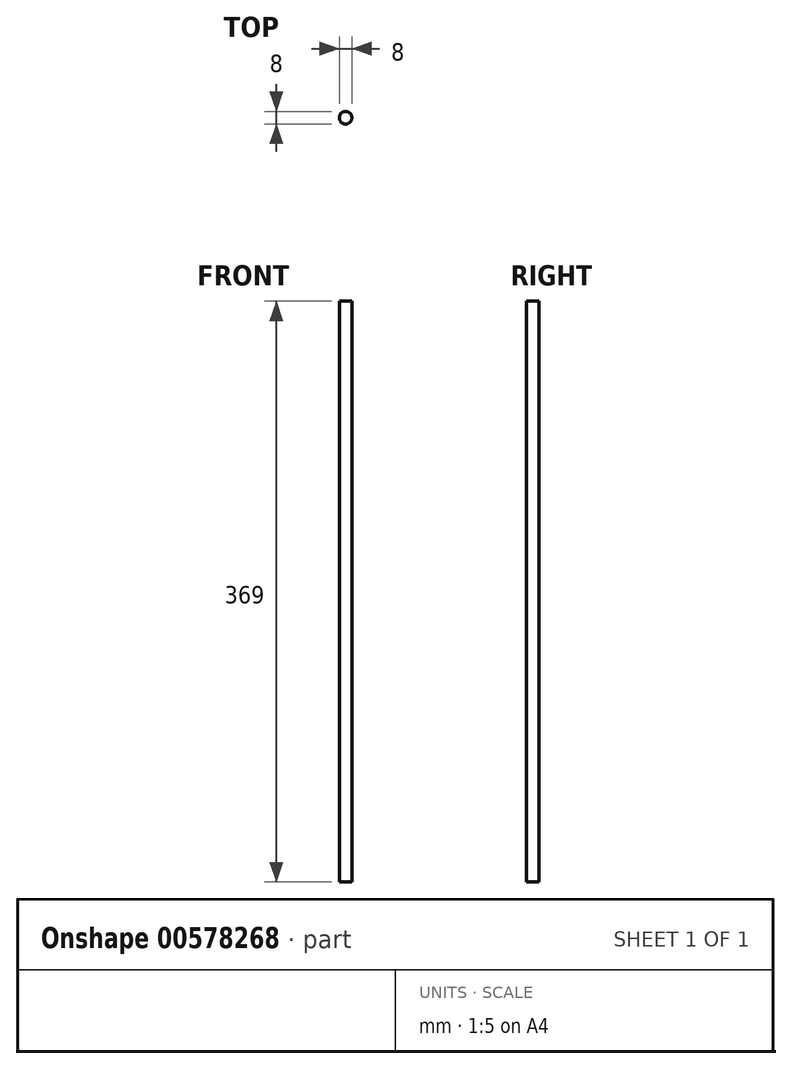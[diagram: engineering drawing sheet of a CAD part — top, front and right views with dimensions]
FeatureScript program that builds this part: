
annotation { "Feature Type Name" : "Feature", "Feature Type Description" : "" }
export const myFeature = defineFeature(function(context is Context, id is Id, definition is map)
    precondition{}
    {
        {
            var Q0;
            Q0=qCreatedBy(makeId("Top.planeOp"),FACE);
            var sketch = newSketch(context, id + "F0", { "sketchPlane" : qUnion([Q0])});
            skCircle(sketch, "E0", {"center": v(0, 0) * mm, "radius": 4 * mm});
            skSolve(sketch);
        }
        {
            var Q0;
            Q0 = qSketchRegion(id + "F0", true);
            extrude(context, id + "F1", {"entities" : qUnion([Q0]), "depth" : 369 * mm, "offsetDistance" : 25 * mm});
        }
    });
